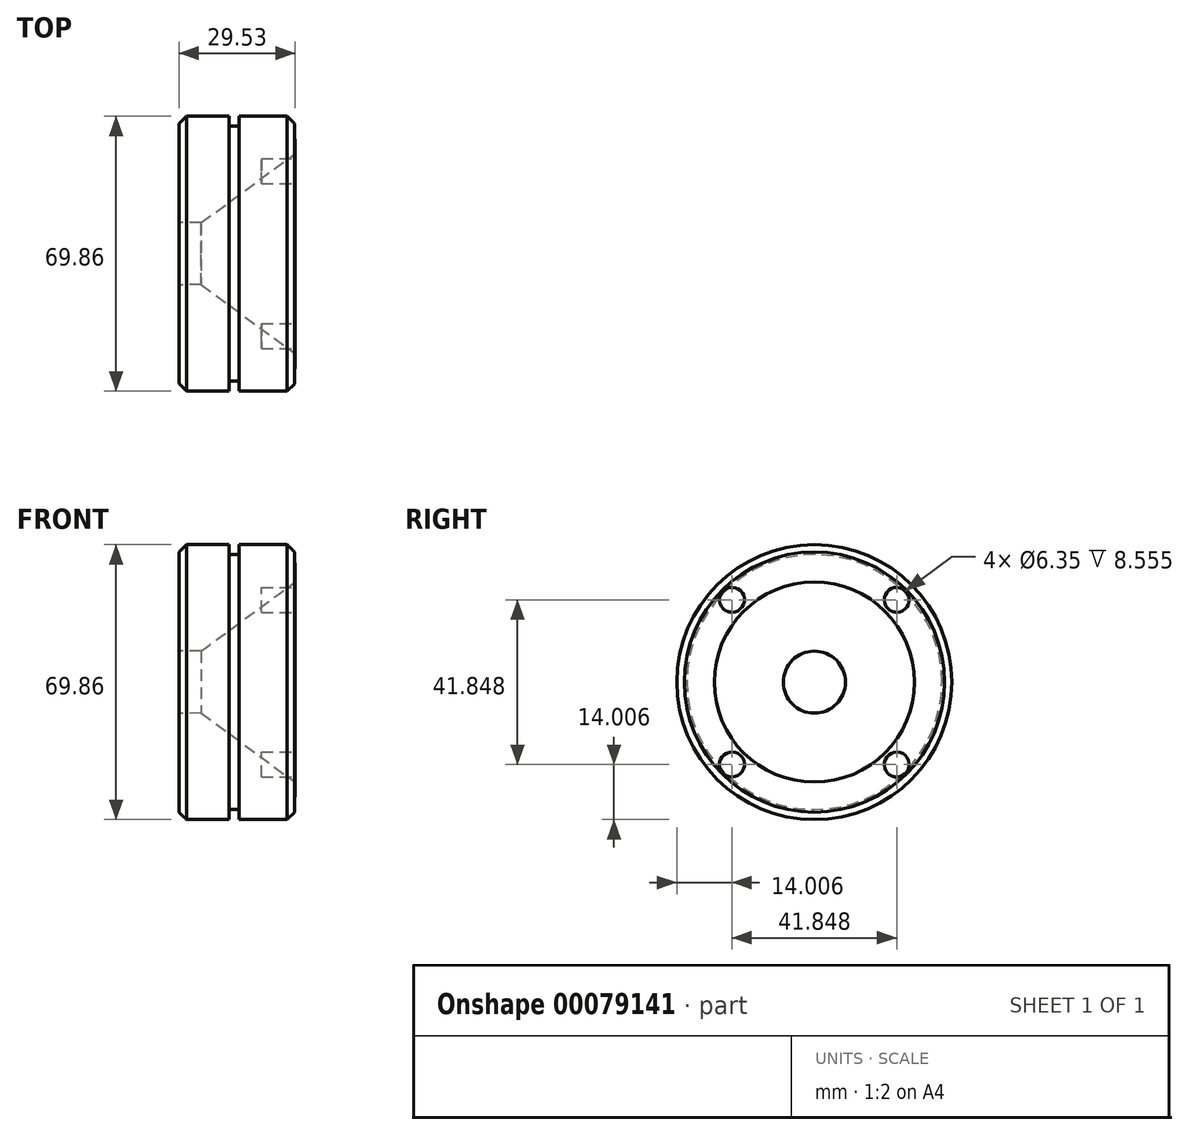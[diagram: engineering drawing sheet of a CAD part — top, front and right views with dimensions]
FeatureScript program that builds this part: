
annotation { "Feature Type Name" : "Feature", "Feature Type Description" : "" }
export const myFeature = defineFeature(function(context is Context, id is Id, definition is map)
    precondition{}
    {
        {
            var Q0;
            Q0=qCreatedBy(makeId("Front.planeOp"),FACE);
            var sketch = newSketch(context, id + "F0", { "sketchPlane" : qUnion([Q0])});
            skLineSegment(sketch, "E0", {"start": v(5.66, 7.89) * mm, "end": v(29.53, 25.4) * mm});
            skLineSegment(sketch, "E1", {"start": v(29.34, 34.93) * mm, "end": v(15.32, 34.93) * mm});
            skLineSegment(sketch, "E2", {"start": v(15.32, 34.93) * mm, "end": v(15.32, 32.39) * mm});
            skLineSegment(sketch, "E3", {"start": v(15.32, 32.39) * mm, "end": v(12.7, 32.39) * mm});
            skLineSegment(sketch, "E4", {"start": v(12.7, 32.39) * mm, "end": v(12.7, 34.93) * mm});
            skLineSegment(sketch, "E5", {"start": v(12.7, 34.93) * mm, "end": v(0, 34.93) * mm});
            skLineSegment(sketch, "E6", {"start": v(0, 34.93) * mm, "end": v(0, 7.94) * mm});
            skLineSegment(sketch, "E7", {"start": v(29.53, 25.4) * mm, "end": v(29.34, 34.93) * mm});
            skLineSegment(sketch, "E8", {"start": v(5.66, 7.89) * mm, "end": v(0, 7.94) * mm});
            skLineSegment(sketch, "E9", {"start": v(0, 0) * mm, "end": v(20.44, 0) * mm});
            skSolve(sketch);
        }
        {
            var Q0;
            Q0=makeQuery(id+"F0.imprint","IMPRINT",FACE,{"disambiguationData":[TD([[makeQuery(id+"F0.imprint","IMPRINT",EDGE,{"derivedFrom":sQuery(id+"F0.wireOp",EDGE,"E0")}),1.0]])]});
            var Q1;
            Q1=sQuery(id+"F0.wireOp",EDGE,"E9");
            revolve(context, id + "F1", {"entities" : qUnion([Q0]), "axis" : qUnion([Q1]), "revolveType" : RevolveType.FULL});
        }
        {
            var Q0;
            Q0=makeQuery(id+"F1.opRevolve","SWEPT_EDGE",EDGE,{"disambiguationData":[OSD([sQuery(id+"F0.wireOp",EDGE,"E5"),sQuery(id+"F0.wireOp",EDGE,"E6")])]});
            var Q1;
            Q1=makeQuery(id+"F1.opRevolve","SWEPT_EDGE",EDGE,{"disambiguationData":[OSD([sQuery(id+"F0.wireOp",EDGE,"E1"),sQuery(id+"F0.wireOp",EDGE,"E7")])]});
            chamfer(context, id + "F2", {"entities" : qUnion([Q0, Q1]), "width" : 1.9 * mm, "tangentPropagation" : true});
        }
        {
            var Q0;
            Q0=qCreatedBy(makeId("Right.planeOp"),FACE);
            cPlane(context, id + "F3", {"entities" : qUnion([Q0]), "cplaneType" : CPlaneType.OFFSET, "offset" : 33.65 * mm, "width" : 152.4 * mm, "height" : 152.4 * mm});
        }
        {
            var Q0;
            Q0=qCreatedBy(id+"F3.planeOp",FACE);
            var sketch = newSketch(context, id + "F4", { "sketchPlane" : qUnion([Q0])});
            skPoint(sketch, "E10.middle", {"position": v(0, 0) * mm});
            skCircle(sketch, "E11", {"center": v(20.92, 20.92) * mm, "radius": 3.18 * mm});
            skCircle(sketch, "E12", {"center": v(20.92, -20.92) * mm, "radius": 3.18 * mm});
            skCircle(sketch, "E13", {"center": v(-20.92, -20.92) * mm, "radius": 3.18 * mm});
            skCircle(sketch, "E14", {"center": v(-20.92, 20.92) * mm, "radius": 3.18 * mm});
            skSolve(sketch);
        }
        {
            var Q0;
            Q0=qSketchRegion(id+"F4",true);
            extrude(context, id + "F5", {"entities" : qUnion([Q0]), "operationType" : NewBodyOperationType.REMOVE, "oppositeDirection" : true, "depth" : 12.7 * mm});
        }
    });
